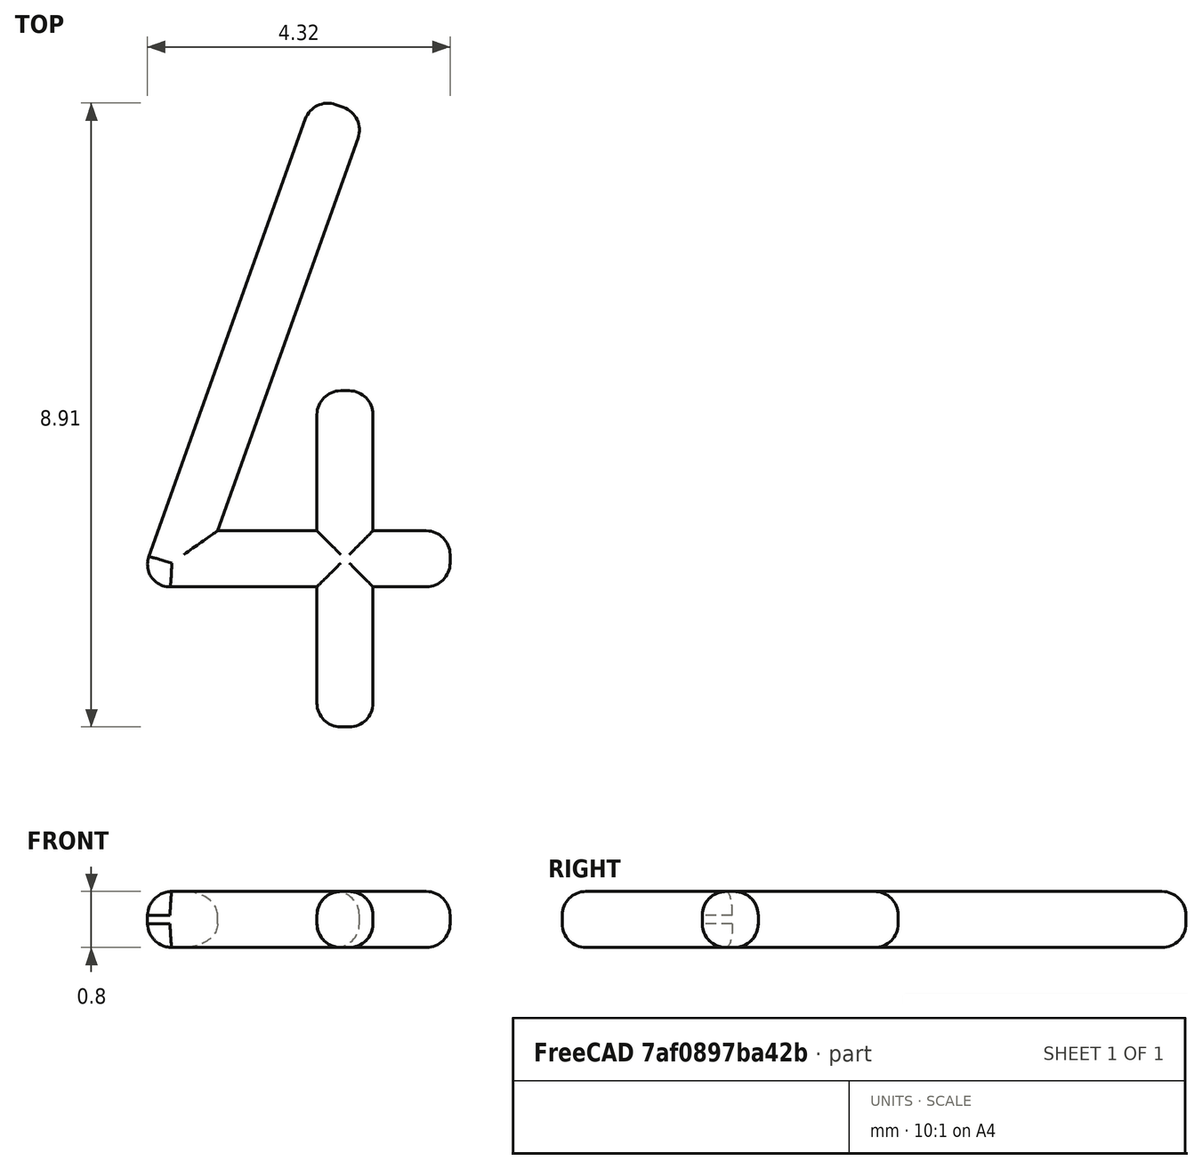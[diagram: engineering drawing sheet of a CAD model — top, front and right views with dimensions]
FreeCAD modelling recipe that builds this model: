
FCSTD DOCUMENT  (FreeCAD 0.16R6712 (Git))
Label: 4
License: All rights reserved
LicenseURL: http://en.wikipedia.org/wiki/All_rights_reserved
objects: Sketcher::SketchObject×1, PartDesign::Pad×1, PartDesign::Fillet×1, Mesh::Feature×1
note: 4 computed .brp shape members not serialized (recipe doc carries the construction recipe); baked Part::Feature solids carry a one-line shape summary decoded from their .brp

FEATURE [Sketcher::SketchObject] Sketch
  sketch-geometry (15):
    g0: LineSegment StartX=0.0466289 StartY=9 StartZ=0 EndX=-2.30084 EndY=2.42883 EndZ=0
    g1: LineSegment StartX=0.8 StartY=8.73087 StartZ=0 EndX=-1.31873 EndY=2.8 EndZ=0
    g2: LineSegment StartX=-1.99866 StartY=2 StartZ=0 EndX=0.1 EndY=2 EndZ=0
    g3: LineSegment StartX=-1.31873 StartY=2.8 StartZ=0 EndX=0.1 EndY=2.8 EndZ=0
    g4: LineSegment StartX=0.0466289 StartY=9 StartZ=0 EndX=0.8 EndY=8.73087 EndZ=0
    g5: LineSegment StartX=0.1 StartY=4.8 StartZ=0 EndX=0.9 EndY=4.8 EndZ=0
    g6: LineSegment StartX=0.9 StartY=4.8 StartZ=0 EndX=0.9 EndY=2.8 EndZ=0
    g7: LineSegment StartX=0.9 StartY=0 StartZ=0 EndX=0.1 EndY=0 EndZ=0
    g8: LineSegment StartX=0.1 StartY=0 StartZ=0 EndX=0.1 EndY=2 EndZ=0
    g9: LineSegment StartX=0.9 StartY=2 StartZ=0 EndX=0.9 EndY=0 EndZ=0
    g10: LineSegment StartX=0.1 StartY=2.8 StartZ=0 EndX=0.1 EndY=4.8 EndZ=0
    g11: LineSegment StartX=0.9 StartY=2.8 StartZ=0 EndX=2 EndY=2.8 EndZ=0
    g12: LineSegment StartX=0.9 StartY=2 StartZ=0 EndX=2 EndY=2 EndZ=0
    g13: LineSegment StartX=2 StartY=2.8 StartZ=0 EndX=2 EndY=2 EndZ=0
    g14: ArcOfCircle CenterX=-1.99866 CenterY=2.32088 CenterZ=0 NormalX=0 NormalY=0 NormalZ=1 Radius=0.320879 StartAngle=2.79849 EndAngle=4.71239
  constraints (40):
    c: Horizontal(g2)
    c: Horizontal(g3)
    c: Coincident(g4,g1)
    c: Coincident(g1,g3)
    c: Perpendicular(g1,g4)
    c: Coincident(g0,g4)
    c: Distance(g0,g1) = 0.8
    c: Distance(g11,g12) = 0.8
    c: Parallel(g0,g1)
    c: Coincident(g5,g6)
    c: Coincident(g9,g7)
    c: Coincident(g7,g8)
    c: Coincident(g10,g5)
    c: Horizontal(g5)
    c: Horizontal(g7)
    c: Vertical(g6)
    c: Vertical(g8)
    c: Coincident(g3,g10)
    c: Coincident(g11,g6)
    c: Tangent(g3,g11)
    c: Coincident(g2,g8)
    c: Coincident(g12,g9)
    c: Tangent(g2,g12)
    c: Distance(g6,g5) = 2
    c: Coincident(g13,g11)
    c: Coincident(g13,g12)
    c: Vertical(g13)
    c: PointOnObject(g7,g-1)
    c: Distance(g7,g12) = 2
    c: DistanceY(g-1,g0) = 9
    c: DistanceX(g-2,g1) = 0.8
    c: Tangent(g0,g14) = -1.5708
    c: Tangent(g2,g14) = -1.5708
    c: DistanceX(g-2,g12) = 2
    c: Distance(g11,g6) = 1.1
    c: Distance(g12,g9) = 1.1
    c: Vertical(g9)
    c: DistanceX(g5,g5) = 0.8
    c: DistanceX(g7,g7) = 0.8
    c: Vertical(g10)
FEATURE [PartDesign::Pad] Pad
  Length = 0.8
  Length2 = 100
  Midplane = true
  Sketch = -> Sketch
  Type = 0
FEATURE [PartDesign::Fillet] Fillet
  Base = -> Pad [Edge4,Edge7,Edge10,Edge13,Edge16,Edge19,Edge22,Edge25,Edge28,Edge31,Edge34,Edge37,Edge40,Edge43,Edge45,Edge3,Edge6,Edge9,Edge12,Edge15,Edge18,Edge21,Edge24,Edge27,Edge30,Edge33,Edge36,Edge39,Edge42,Edge44,Edge26,Edge23,Edge35,Edge32,Edge1,Edge2,Edge17,Edge14]
  Radius = 0.34
FEATURE [Mesh::Feature] Mesh  label="Fillet (Meshed)"
